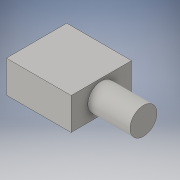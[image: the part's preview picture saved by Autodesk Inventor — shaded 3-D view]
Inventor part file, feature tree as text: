
AUTODESK INVENTOR PART (.ipt)
format: ipt  version: 2016 (Build 200138000, 138)  size: 100,352 bytes
history: native  units: in
note: dims shown in document units (in); Inventor stores cm internally (conversion verified against a paired STEP export)
features: sketch x3, extrude x2
ambient origin geometry x8: Origin, YZ Plane, XZ Plane, XY Plane, X Axis, Y Axis, Z Axis, Center Point
bodies: Solid1 (feature_tree)
feature tree (5):
  extrude  "Extrusion1"  Depth=0.266in
  sketch  "Sketch2"  dims[d2=0.538in d3=0.0in d5=0.35in d6=0.0in]
  extrude  "Extrusion2"  Depth=0.35in TaperAngle=0.0deg
  sketch  "Sketch1"  dims[d0=0.502in d1=0.266in]
  sketch  "Sketch3"  dims[d7=0.251in d8=0.133in d9=0.224in]
